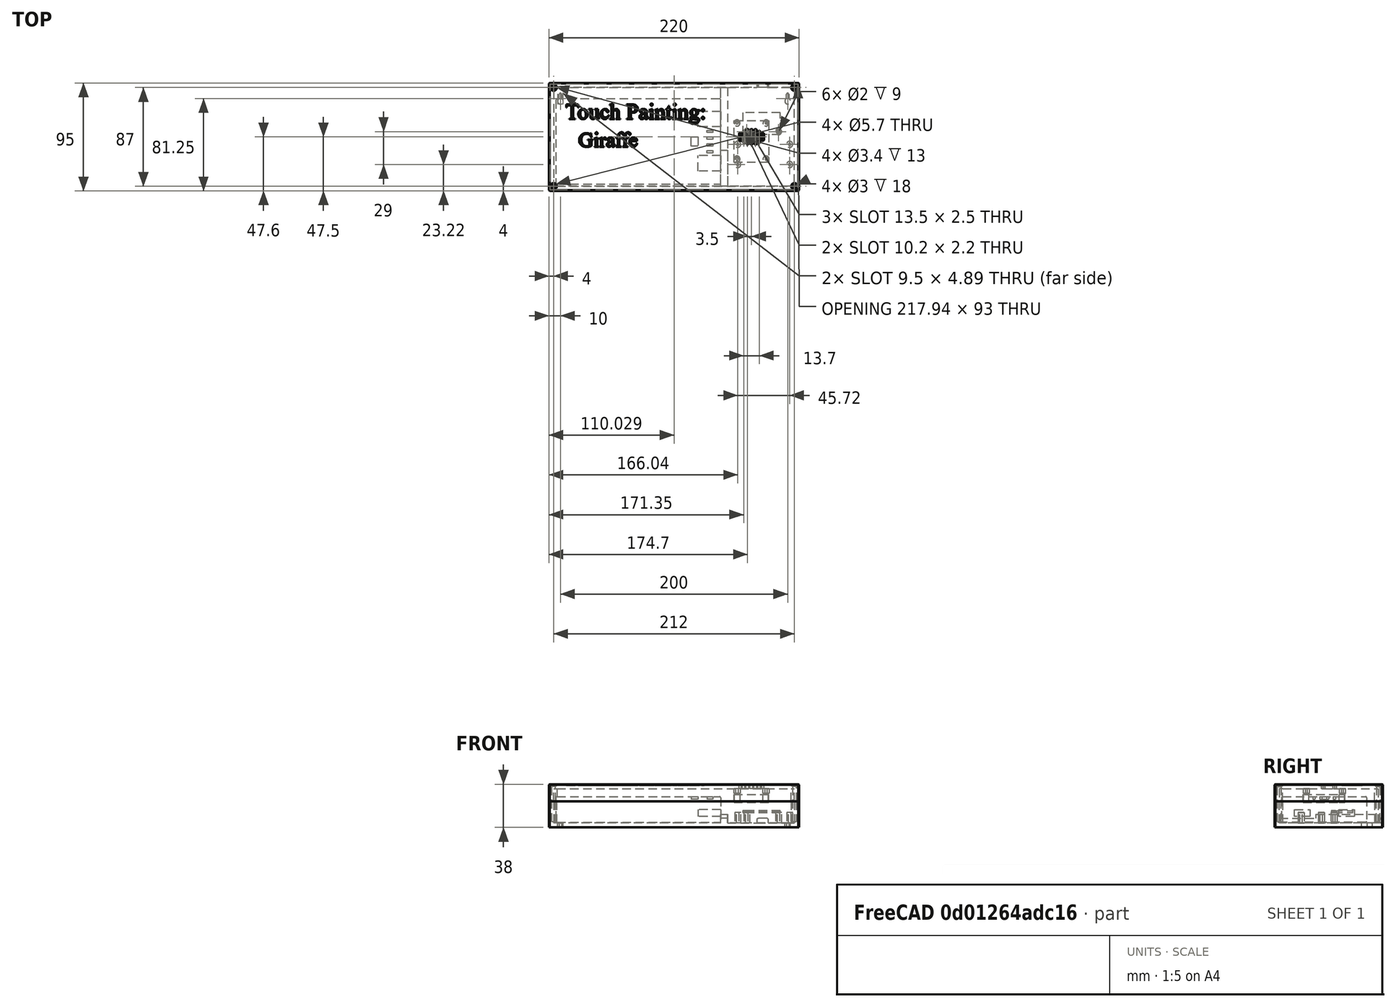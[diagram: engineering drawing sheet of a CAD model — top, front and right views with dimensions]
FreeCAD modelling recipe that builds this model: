
FCSTD DOCUMENT  (FreeCAD 0.19R24276 (Git))
Label: ShortBox
License: All rights reserved
LicenseURL: http://en.wikipedia.org/wiki/All_rights_reserved
objects: Sketcher::SketchObject×17, PartDesign::Pocket×12, PartDesign::Pad×7, PartDesign::Chamfer×4, Part::Feature×3, Mesh::Feature×2, PartDesign::Body×2, Part::Part2DObjectPython×2
note: 70 computed .brp shape members not serialized (recipe doc carries the construction recipe); baked Part::Feature solids carry a one-line shape summary decoded from their .brp

FEATURE [Part::Feature] Solid  label="MPR121 v1"
  Placement = pos=(170.5,49.7,13) rot=(0,0,1;0rad)
  shape: bbox 33.02 x 19.05 x 1.6 mm, 10 faces (baked)
FEATURE [Mesh::Feature] _062_nRF52830_Feather  label="4062-nRF52830-Feather"
  Placement = pos=(162.5,20.7,13) rot=(0,0,1;0rad)
FEATURE [Part::Feature] Solid001  label="Pocket001"
  Placement = pos=(78.6,43.5,27) rot=(1,0,0;3.14159rad)
  shape: bbox 145 x 75 x 22.5 mm, 61 faces (baked)
FEATURE [Sketcher::SketchObject] Sketch
  FullyConstrained = true
  sketch-geometry (4):
    g0: LineSegment StartX=0 StartY=0 StartZ=0 EndX=220 EndY=0 EndZ=0
    g1: LineSegment StartX=220 StartY=0 StartZ=0 EndX=220 EndY=95 EndZ=0
    g2: LineSegment StartX=220 StartY=95 StartZ=0 EndX=0 EndY=95 EndZ=0
    g3: LineSegment StartX=0 StartY=95 StartZ=0 EndX=0 EndY=0 EndZ=0
  constraints (11):
    c: Coincident(g0,g1)
    c: Coincident(g1,g2)
    c: Coincident(g2,g3)
    c: Coincident(g3,g0)
    c: Horizontal(g0)
    c: Horizontal(g2)
    c: Vertical(g1)
    c: Vertical(g3)
    c: Coincident(g0,g-1)
    c: DistanceX(g2,g2) = 220
    c: DistanceY(g1,g1) = 95
FEATURE [Part::Feature] Solid002  label="Speaker"
  Placement = pos=(178,43.4,22) rot=(0,0,1;0rad)
  shape: bbox 30.48 x 36.83 x 7 mm, 10 faces (baked)
FEATURE [PartDesign::Pad] Pad
  Direction = (1,1,1)
  Length = 23
  Length2 = 100
  Profile = -> Sketch
  Type = 0
FEATURE [Sketcher::SketchObject] Sketch001
  ExternalGeometry = -> [Pad]
  FullyConstrained = true
  MapMode = 5
  Placement = pos=(0,0,23) rot=(0,0,1;0rad)
  Support = -> [Pad]
  sketch-geometry (4):
    g0: LineSegment StartX=4 StartY=91 StartZ=0 EndX=216 EndY=91 EndZ=0
    g1: LineSegment StartX=216 StartY=91 StartZ=0 EndX=216 EndY=4 EndZ=0
    g2: LineSegment StartX=216 StartY=4 StartZ=0 EndX=4 EndY=4 EndZ=0
    g3: LineSegment StartX=4 StartY=4 StartZ=0 EndX=4 EndY=91 EndZ=0
  constraints (12):
    c: Coincident(g0,g1)
    c: Coincident(g1,g2)
    c: Coincident(g2,g3)
    c: Coincident(g3,g0)
    c: Horizontal(g0)
    c: Horizontal(g2)
    c: Vertical(g1)
    c: Vertical(g3)
    c: DistanceY(g0,g-3) = 4
    c: DistanceX(g-3,g0) = 4
    c: DistanceY(g-1,g2) = 4
    c: DistanceX(g1,g-4) = 4
FEATURE [PartDesign::Pocket] Pocket
  BaseFeature = -> Pad
  Length = 19
  Length2 = 100
  Profile = -> Sketch001
  Type = 0
FEATURE [Sketcher::SketchObject] Sketch002
  ExternalGeometry = -> [Pocket]
  FullyConstrained = true
  MapMode = 5
  Placement = pos=(0,0,4) rot=(0,0,1;0rad)
  Support = -> [Pocket]
  sketch-geometry (6):
    g0: Circle CenterX=174.04 CenterY=52.22 CenterZ=0 NormalX=0 NormalY=0 NormalZ=1 AngleXU=0 Radius=2.7
    g1: Circle CenterX=201.98 CenterY=52.22 CenterZ=0 NormalX=0 NormalY=0 NormalZ=1 AngleXU=0 Radius=2.7
    g2: Circle CenterX=166.04 CenterY=41 CenterZ=0 NormalX=0 NormalY=0 NormalZ=1 AngleXU=0 Radius=2.7
    g3: Circle CenterX=166.04 CenterY=23.22 CenterZ=0 NormalX=0 NormalY=0 NormalZ=1 AngleXU=0 Radius=2.7
    g4: Circle CenterX=211.76 CenterY=23.22 CenterZ=0 NormalX=0 NormalY=0 NormalZ=1 AngleXU=0 Radius=2.7
    g5: Circle CenterX=211.76 CenterY=41 CenterZ=0 NormalX=0 NormalY=0 NormalZ=1 AngleXU=0 Radius=2.7
  constraints (18):
    c: DistanceX(g5,g-5) = 4.24
    c: DistanceY(g5,g-5) = 50
    c: Radius(g5) = 2.7
    c: Radius(g2) = 2.7
    c: Radius(g3) = 2.7
    c: Radius(g4) = 2.7
    c: DistanceX(g2,g3) = 0
    c: DistanceY(g3,g4) = 0
    c: DistanceY(g5,g2) = 0
    c: DistanceX(g2,g5) = 45.72
    c: DistanceY(g3,g2) = 17.78
    c: Radius(g0) = 2.7
    c: Radius(g1) = 2.7
    c: DistanceY(g0,g1) = 0
    c: DistanceX(g0,g1) = 27.94
    c: DistanceY(g2,g0) = 11.22
    c: DistanceX(g4,g5) = 0
    c: DistanceX(g0,g2) = -8
FEATURE [PartDesign::Pad] Pad001  label="BoardPosts"
  BaseFeature = -> Pocket
  Direction = (1,1,1)
  Length = 9
  Length2 = 100
  Profile = -> Sketch002
  Type = 0
FEATURE [Sketcher::SketchObject] Sketch003
  ExternalGeometry = -> [Pad001]
  FullyConstrained = true
  MapMode = 5
  Placement = pos=(0,0,13) rot=(0,0,1;0rad)
  Support = -> [Pad001]
  sketch-geometry (6):
    g0: Circle CenterX=166.04 CenterY=41 CenterZ=0 NormalX=0 NormalY=0 NormalZ=1 AngleXU=0 Radius=1
    g1: Circle CenterX=211.76 CenterY=41 CenterZ=0 NormalX=0 NormalY=0 NormalZ=1 AngleXU=0 Radius=1
    g2: Circle CenterX=211.76 CenterY=23.22 CenterZ=0 NormalX=0 NormalY=0 NormalZ=1 AngleXU=0 Radius=1
    g3: Circle CenterX=166.04 CenterY=23.22 CenterZ=0 NormalX=0 NormalY=0 NormalZ=1 AngleXU=0 Radius=1
    g4: Circle CenterX=174.04 CenterY=52.22 CenterZ=0 NormalX=0 NormalY=0 NormalZ=1 AngleXU=0 Radius=1
    g5: Circle CenterX=201.98 CenterY=52.22 CenterZ=0 NormalX=0 NormalY=0 NormalZ=1 AngleXU=0 Radius=1
  constraints (12):
    c: Coincident(g0,g-6)
    c: Coincident(g1,g-5)
    c: Coincident(g2,g-8)
    c: Coincident(g3,g-7)
    c: Coincident(g4,g-3)
    c: Coincident(g5,g-4)
    c: Radius(g4) = 1
    c: Radius(g5) = 1
    c: Radius(g1) = 1
    c: Radius(g0) = 1
    c: Radius(g3) = 1
    c: Radius(g2) = 1
FEATURE [PartDesign::Pocket] Pocket001  label="BoardPostHoles"
  BaseFeature = -> Pad001
  Length = 9
  Length2 = 100
  Profile = -> Sketch003
  Type = 0
FEATURE [Sketcher::SketchObject] Sketch004
  ExternalGeometry = -> [Pocket001]
  FullyConstrained = true
  MapMode = 5
  Placement = pos=(0,95,0) rot=(0,0.707107,0.707107;3.14159rad)
  Support = -> [Pocket001]
  sketch-geometry (4):
    g0: LineSegment StartX=-193.01 StartY=8 StartZ=0 EndX=-183.01 EndY=8 EndZ=0
    g1: LineSegment StartX=-183.01 StartY=8 StartZ=0 EndX=-183.01 EndY=4 EndZ=0
    g2: LineSegment StartX=-183.01 StartY=4 StartZ=0 EndX=-193.01 EndY=4 EndZ=0
    g3: LineSegment StartX=-193.01 StartY=4 StartZ=0 EndX=-193.01 EndY=8 EndZ=0
  constraints (13):
    c: Coincident(g0,g1)
    c: Coincident(g1,g2)
    c: Coincident(g2,g3)
    c: Coincident(g3,g0)
    c: Horizontal(g0)
    c: Horizontal(g2)
    c: Vertical(g1)
    c: Vertical(g3)
    c: PointOnObject(g1,g-3)
    c: DistanceX(g0,g0) = 10
    c: DistanceX(g-5,g-6) = 22.54
    c: DistanceX(g-5,g0) = 6.27
    c: DistanceY(g1,g1) = 4
FEATURE [PartDesign::Pocket] Pocket002  label="PaintingWires"
  BaseFeature = -> Pocket001
  Length = 4
  Length2 = 100
  Profile = -> Sketch004
  Type = 0
FEATURE [PartDesign::Chamfer] Chamfer
  Angle = 45
  Base = -> Pocket002 [Edge34,Edge33]
  BaseFeature = -> Pocket002
  ChamferType = 0
  FlipDirection = false
  Size = 1
  Size2 = 1
  SupportTransform = false
FEATURE [Mesh::Feature] TalenCell_battery_pack
  Placement = pos=(5,154,-68) rot=(1,0,0;1.5708rad)
FEATURE [Sketcher::SketchObject] Sketch006
  FullyConstrained = false
  MapMode = 5
  Placement = pos=(0,0,4) rot=(0,0,1;0rad)
  sketch-geometry (4):
    g0: LineSegment StartX=151 StartY=91 StartZ=0 EndX=157 EndY=91 EndZ=0
    g1: LineSegment StartX=157 StartY=91 StartZ=0 EndX=157 EndY=3.51944 EndZ=0
    g2: LineSegment StartX=157 StartY=3.51944 StartZ=0 EndX=151 EndY=3.51944 EndZ=0
    g3: LineSegment StartX=151 StartY=3.51944 StartZ=0 EndX=151 EndY=91 EndZ=0
  constraints (9):
    c: Coincident(g0,g1)
    c: Coincident(g1,g2)
    c: Coincident(g2,g3)
    c: Coincident(g3,g0)
    c: Horizontal(g0)
    c: Horizontal(g2)
    c: Vertical(g1)
    c: Vertical(g3)
    c: DistanceX(g0,g0) = 6
FEATURE [PartDesign::Pad] Pad002  label="BatDivider"
  BaseFeature = -> Chamfer
  Direction = (1,1,1)
  Length = 7.5
  Length2 = 100
  Profile = -> Sketch006
  Type = 0
FEATURE [Sketcher::SketchObject] Sketch007
  ExternalGeometry = -> [Pad002]
  FullyConstrained = true
  MapMode = 5
  Placement = pos=(0,0,11.5) rot=(0,0,1;0rad)
  Support = -> [Pad002]
  sketch-geometry (4):
    g0: LineSegment StartX=151 StartY=36 StartZ=0 EndX=157 EndY=36 EndZ=0
    g1: LineSegment StartX=157 StartY=36 StartZ=0 EndX=157 EndY=4 EndZ=0
    g2: LineSegment StartX=157 StartY=4 StartZ=0 EndX=151 EndY=4 EndZ=0
    g3: LineSegment StartX=151 StartY=4 StartZ=0 EndX=151 EndY=36 EndZ=0
  constraints (11):
    c: Coincident(g0,g1)
    c: Coincident(g1,g2)
    c: Coincident(g2,g3)
    c: Coincident(g3,g0)
    c: Horizontal(g0)
    c: Horizontal(g2)
    c: Vertical(g1)
    c: Vertical(g3)
    c: PointOnObject(g0,g-3)
    c: Coincident(g1,g-4)
    c: DistanceY(g1,g1) = 32
FEATURE [PartDesign::Pocket] Pocket003  label="BatDividerUsbCutout"
  BaseFeature = -> Pad002
  Length = 3.5
  Length2 = 100
  Profile = -> Sketch007
  Type = 0
FEATURE [Sketcher::SketchObject] Sketch008
  ExternalGeometry = -> [Pocket003]
  FullyConstrained = false
  MapMode = 5
  Placement = pos=(0,0,4) rot=(0,0,1;0rad)
  Support = -> [Pocket003]
  sketch-geometry (8):
    g0: ArcOfCircle CenterX=10 CenterY=85 CenterZ=0 NormalX=0 NormalY=0 NormalZ=1 AngleXU=0 Radius=1 StartAngle=0 EndAngle=3.14159
    g1: ArcOfCircle CenterX=10 CenterY=79 CenterZ=0 NormalX=0 NormalY=0 NormalZ=1 AngleXU=0 Radius=2.5 StartAngle=1.98231 EndAngle=7.44246
    g2: LineSegment StartX=11 StartY=85 StartZ=0 EndX=11 EndY=81.2913 EndZ=0
    g3: LineSegment StartX=9 StartY=81.2913 StartZ=0 EndX=9 EndY=85 EndZ=0
    g4: ArcOfCircle CenterX=210 CenterY=85 CenterZ=0 NormalX=0 NormalY=0 NormalZ=1 AngleXU=0 Radius=1 StartAngle=0 EndAngle=3.14159
    g5: ArcOfCircle CenterX=210 CenterY=79 CenterZ=0 NormalX=0 NormalY=0 NormalZ=1 AngleXU=0 Radius=2.5 StartAngle=1.98231 EndAngle=7.44246
    g6: LineSegment StartX=211 StartY=85 StartZ=0 EndX=211 EndY=81.2913 EndZ=0
    g7: LineSegment StartX=209 StartY=81.2913 StartZ=0 EndX=209 EndY=85 EndZ=0
  constraints (25):
    c: Vertical(g2)
    c: Vertical(g3)
    c: Radius(g0) = 1
    c: Radius(g1) = 2.5
    c: DistanceX(g3,g2) = 2
    c: DistanceY(g2,g0) = 0
    c: DistanceX(g3,g0) = 1
    c: DistanceY(g1,g0) = 6
    c: DistanceX(g0,g1) = 0
    c: DistanceY(g0,g-4) = 6
    c: DistanceX(g-4,g0) = 6
    c: Coincident(g1,g3)
    c: Coincident(g1,g2)
    c: Vertical(g6)
    c: Vertical(g7)
    c: DistanceY(g7,g4) = 0
    c: Radius(g5) = 2.5
    c: Radius(g4) = 1
    c: DistanceX(g7,g6) = 2
    c: DistanceX(g7,g4) = 1
    c: DistanceY(g5,g4) = 6
    c: DistanceY(g4,g-6) = 6
    c: DistanceX(g4,g-6) = 6
    c: Coincident(g5,g7)
    c: Coincident(g5,g6)
FEATURE [PartDesign::Pocket] Pocket004  label="HangerHoles"
  BaseFeature = -> Pocket003
  Length = 4
  Length2 = 100
  Profile = -> Sketch008
  Type = 0
FEATURE [Sketcher::SketchObject] Sketch009
  ExternalGeometry = -> [Pocket004]
  FullyConstrained = true
  MapMode = 5
  Placement = pos=(0,0,4) rot=(0,0,1;0rad)
  Support = -> [Pocket004]
  sketch-geometry (4):
    g0: Circle CenterX=4 CenterY=91 CenterZ=0 NormalX=0 NormalY=0 NormalZ=1 AngleXU=0 Radius=3
    g1: Circle CenterX=4 CenterY=4 CenterZ=0 NormalX=0 NormalY=0 NormalZ=1 AngleXU=0 Radius=3
    g2: Circle CenterX=216 CenterY=4 CenterZ=0 NormalX=0 NormalY=0 NormalZ=1 AngleXU=0 Radius=3
    g3: Circle CenterX=216 CenterY=91 CenterZ=0 NormalX=0 NormalY=0 NormalZ=1 AngleXU=0 Radius=3
  constraints (8):
    c: Coincident(g0,g-4)
    c: Radius(g0) = 3
    c: Coincident(g1,g-4)
    c: Radius(g1) = 3
    c: Coincident(g2,g-5)
    c: Radius(g2) = 3
    c: Coincident(g3,g-5)
    c: Radius(g3) = 3
FEATURE [PartDesign::Pad] Pad003  label="TopMountingPosts"
  BaseFeature = -> Pocket004
  Direction = (1,1,1)
  Length = 19
  Length2 = 100
  Profile = -> Sketch009
  Type = 0
FEATURE [Sketcher::SketchObject] Sketch010
  ExternalGeometry = -> [Pad003]
  FullyConstrained = true
  MapMode = 5
  Placement = pos=(0,0,23) rot=(0,0,1;0rad)
  Support = -> [Pad003]
  sketch-geometry (4):
    g0: Circle CenterX=216 CenterY=91 CenterZ=0 NormalX=0 NormalY=0 NormalZ=1 AngleXU=0 Radius=1.5
    g1: Circle CenterX=216 CenterY=4 CenterZ=0 NormalX=0 NormalY=0 NormalZ=1 AngleXU=0 Radius=1.5
    g2: Circle CenterX=4 CenterY=4 CenterZ=0 NormalX=0 NormalY=0 NormalZ=1 AngleXU=0 Radius=1.5
    g3: Circle CenterX=4 CenterY=91 CenterZ=0 NormalX=0 NormalY=0 NormalZ=1 AngleXU=0 Radius=1.5
  constraints (8):
    c: Coincident(g0,g-5)
    c: Coincident(g1,g-6)
    c: Coincident(g2,g-4)
    c: Coincident(g3,g-3)
    c: Radius(g3) = 1.5
    c: Radius(g2) = 1.5
    c: Radius(g1) = 1.5
    c: Radius(g0) = 1.5
FEATURE [PartDesign::Pocket] Pocket005  label="TopMountingHoles"
  BaseFeature = -> Pad003
  Length = 18
  Length2 = 100
  Profile = -> Sketch010
  Type = 0
FEATURE [Sketcher::SketchObject] Sketch011
  FullyConstrained = true
  MapMode = 5
  Support = -> [XY_Plane001]
  sketch-geometry (4):
    g0: LineSegment StartX=0 StartY=95 StartZ=0 EndX=220 EndY=95 EndZ=0
    g1: LineSegment StartX=220 StartY=95 StartZ=0 EndX=220 EndY=0 EndZ=0
    g2: LineSegment StartX=220 StartY=0 StartZ=0 EndX=0 EndY=0 EndZ=0
    g3: LineSegment StartX=0 StartY=0 StartZ=0 EndX=0 EndY=95 EndZ=0
  constraints (12):
    c: Coincident(g0,g1)
    c: Coincident(g1,g2)
    c: Coincident(g2,g3)
    c: Coincident(g3,g0)
    c: Horizontal(g0)
    c: Horizontal(g2)
    c: Vertical(g1)
    c: Vertical(g3)
    c: PointOnObject(g0,g-2)
    c: DistanceX(g0,g0) = 220
    c: DistanceY(g3,g3) = 95
    c: DistanceY(g2,g-1) = 0
FEATURE [PartDesign::Pad] Pad004
  Direction = (1,1,1)
  Length = 15
  Length2 = 100
  Profile = -> Sketch011
  Type = 0
FEATURE [Sketcher::SketchObject] Sketch012
  ExternalGeometry = -> [Pad004]
  FullyConstrained = true
  MapMode = 5
  Placement = pos=(0,0,0) rot=(1,0,0;3.14159rad)
  Support = -> [Pad004]
  sketch-geometry (4):
    g0: LineSegment StartX=4 StartY=-4 StartZ=0 EndX=216 EndY=-4 EndZ=0
    g1: LineSegment StartX=216 StartY=-4 StartZ=0 EndX=216 EndY=-91 EndZ=0
    g2: LineSegment StartX=216 StartY=-91 StartZ=0 EndX=4 EndY=-91 EndZ=0
    g3: LineSegment StartX=4 StartY=-91 StartZ=0 EndX=4 EndY=-4 EndZ=0
  constraints (13):
    c: Coincident(g0,g1)
    c: Coincident(g1,g2)
    c: Coincident(g2,g3)
    c: Coincident(g3,g0)
    c: Horizontal(g0)
    c: Horizontal(g2)
    c: Vertical(g1)
    c: Vertical(g3)
    c: DistanceY(g0,g-1) = 4
    c: DistanceY(g-3,g1) = 4
    c: DistanceX(g-4,g2) = 4
    c: DistanceX(g-3,g-3) = 0
    c: DistanceX(g0,g-3) = 4
FEATURE [PartDesign::Pocket] Pocket006
  BaseFeature = -> Pad004
  Length = 11
  Length2 = 100
  Profile = -> Sketch012
  Type = 0
FEATURE [Sketcher::SketchObject] Sketch013
  ExternalGeometry = -> [Pocket006]
  FullyConstrained = true
  MapMode = 5
  Placement = pos=(0,0,11) rot=(1,0,0;3.14159rad)
  Support = -> [Pocket006]
  sketch-geometry (4):
    g0: Circle CenterX=4 CenterY=-91 CenterZ=0 NormalX=0 NormalY=0 NormalZ=1 AngleXU=0 Radius=3
    g1: Circle CenterX=4 CenterY=-4 CenterZ=0 NormalX=0 NormalY=0 NormalZ=1 AngleXU=0 Radius=3
    g2: Circle CenterX=216 CenterY=-91 CenterZ=0 NormalX=0 NormalY=0 NormalZ=1 AngleXU=0 Radius=3
    g3: Circle CenterX=216 CenterY=-4 CenterZ=0 NormalX=0 NormalY=0 NormalZ=1 AngleXU=0 Radius=3
  constraints (8):
    c: Coincident(g0,g-4)
    c: Coincident(g1,g-3)
    c: Radius(g1) = 3
    c: Radius(g0) = 3
    c: Coincident(g2,g-4)
    c: Coincident(g3,g-3)
    c: Radius(g3) = 3
    c: Radius(g2) = 3
FEATURE [PartDesign::Pad] Pad005  label="TopMountingPost"
  BaseFeature = -> Pocket006
  Direction = (1,1,1)
  Length = 11
  Length2 = 100
  Profile = -> Sketch013
  Type = 0
FEATURE [Sketcher::SketchObject] Sketch014
  ExternalGeometry = -> [Pad005]
  FullyConstrained = true
  MapMode = 5
  Placement = pos=(0,0,0) rot=(1,0,0;3.14159rad)
  Support = -> [Pad005]
  sketch-geometry (4):
    g0: Circle CenterX=216 CenterY=-4 CenterZ=0 NormalX=0 NormalY=0 NormalZ=1 AngleXU=0 Radius=1.7
    g1: Circle CenterX=216 CenterY=-91 CenterZ=0 NormalX=0 NormalY=0 NormalZ=1 AngleXU=0 Radius=1.7
    g2: Circle CenterX=4 CenterY=-91 CenterZ=0 NormalX=0 NormalY=0 NormalZ=1 AngleXU=0 Radius=1.7
    g3: Circle CenterX=4 CenterY=-4 CenterZ=0 NormalX=0 NormalY=0 NormalZ=1 AngleXU=0 Radius=1.7
  constraints (8):
    c: Coincident(g0,g-6)
    c: Coincident(g1,g-5)
    c: Coincident(g2,g-4)
    c: Coincident(g3,g-3)
    c: Radius(g3) = 1.7
    c: Radius(g2) = 1.7
    c: Radius(g1) = 1.7
    c: Radius(g0) = 1.7
FEATURE [PartDesign::Pocket] Pocket007  label="TopMountingHoles001"
  BaseFeature = -> Pad005
  Length = 15
  Length2 = 100
  Profile = -> Sketch014
  Type = 0
FEATURE [Sketcher::SketchObject] Sketch015
  ExternalGeometry = -> [Pocket007]
  FullyConstrained = true
  MapMode = 5
  Placement = pos=(0,0,15) rot=(0,0,1;0rad)
  Support = -> [Pocket007]
  sketch-geometry (4):
    g0: Circle CenterX=4 CenterY=4 CenterZ=0 NormalX=0 NormalY=0 NormalZ=1 AngleXU=0 Radius=2.85
    g1: Circle CenterX=4 CenterY=91 CenterZ=0 NormalX=0 NormalY=0 NormalZ=1 AngleXU=0 Radius=2.85
    g2: Circle CenterX=216 CenterY=91 CenterZ=0 NormalX=0 NormalY=0 NormalZ=1 AngleXU=0 Radius=2.85
    g3: Circle CenterX=216 CenterY=4 CenterZ=0 NormalX=0 NormalY=0 NormalZ=1 AngleXU=0 Radius=2.85
  constraints (8):
    c: Coincident(g0,g-6)
    c: Radius(g0) = 2.85
    c: Coincident(g1,g-3)
    c: Radius(g1) = 2.85
    c: Coincident(g2,g-4)
    c: Radius(g2) = 2.85
    c: Coincident(g3,g-5)
    c: Radius(g3) = 2.85
FEATURE [PartDesign::Pocket] Pocket008  label="TopMountingHolesHead"
  BaseFeature = -> Pocket007
  Length = 2
  Length2 = 100
  Profile = -> Sketch015
  Type = 0
FEATURE [PartDesign::Chamfer] Chamfer001  label="TopMountingHolesHeadChamf"
  Angle = 45
  Base = -> Pocket008 [Edge60,Edge58,Edge54,Edge56]
  BaseFeature = -> Pocket008
  ChamferType = 0
  FlipDirection = false
  Size = 1.1
  Size2 = 1
  SupportTransform = false
FEATURE [Sketcher::SketchObject] Sketch016
  ExternalGeometry = -> [Chamfer001]
  FullyConstrained = true
  MapMode = 5
  Placement = pos=(0,0,11) rot=(1,0,0;3.14159rad)
  Support = -> [Chamfer001]
  sketch-geometry (8):
    g0: Circle CenterX=165.4 CenterY=-28 CenterZ=0 NormalX=0 NormalY=0 NormalZ=1 AngleXU=0 Radius=2.7
    g1: Circle CenterX=191 CenterY=-28 CenterZ=0 NormalX=0 NormalY=0 NormalZ=1 AngleXU=0 Radius=2.7
    g2: Circle CenterX=191 CenterY=-59.8 CenterZ=0 NormalX=0 NormalY=0 NormalZ=1 AngleXU=0 Radius=2.7
    g3: Circle CenterX=165.4 CenterY=-59.8 CenterZ=0 NormalX=0 NormalY=0 NormalZ=1 AngleXU=0 Radius=2.7
    g4: Circle CenterX=165.4 CenterY=-28 CenterZ=0 NormalX=0 NormalY=0 NormalZ=1 AngleXU=0 Radius=0.9
    g5: Circle CenterX=191 CenterY=-28 CenterZ=0 NormalX=0 NormalY=0 NormalZ=1 AngleXU=0 Radius=0.9
    g6: Circle CenterX=191 CenterY=-59.8 CenterZ=0 NormalX=0 NormalY=0 NormalZ=1 AngleXU=0 Radius=0.9
    g7: Circle CenterX=165.4 CenterY=-59.8 CenterZ=0 NormalX=0 NormalY=0 NormalZ=1 AngleXU=0 Radius=0.9
  constraints (20):
    c: Radius(g0) = 2.7
    c: Radius(g1) = 2.7
    c: Radius(g3) = 2.7
    c: Radius(g2) = 2.7
    c: Coincident(g4,g0)
    c: Coincident(g5,g1)
    c: Coincident(g6,g2)
    c: Coincident(g7,g3)
    c: Radius(g4) = 0.9
    c: Radius(g5) = 0.9
    c: Radius(g7) = 0.9
    c: Radius(g6) = 0.9
    c: DistanceX(g0,g3) = 0
    c: DistanceX(g1,g2) = 0
    c: DistanceY(g3,g2) = 0
    c: DistanceY(g0,g1) = 0
    c: DistanceX(g0,g1) = 25.6
    c: DistanceY(g3,g0) = 31.8
    c: DistanceX(g1,g-3) = 25
    c: DistanceY(g1,g-3) = 24
FEATURE [PartDesign::Pad] Pad006  label="SpeakerPosts"
  BaseFeature = -> Chamfer001
  Direction = (1,1,1)
  Length = 4
  Length2 = 100
  Profile = -> Sketch016
  Type = 0
FEATURE [Sketcher::SketchObject] Sketch017
  ExternalGeometry = -> [Pad006]
  FullyConstrained = true
  MapMode = 5
  Placement = pos=(0,0,11) rot=(1,0,0;3.14159rad)
  Support = -> [Pad006]
  sketch-geometry (28):
    g0: ArcOfCircle CenterX=171.35 CenterY=-43.6 CenterZ=0 NormalX=0 NormalY=0 NormalZ=1 AngleXU=0 Radius=1.1 StartAngle=8e-16 EndAngle=3.14159
    g1: ArcOfCircle CenterX=171.35 CenterY=-51.6 CenterZ=0 NormalX=0 NormalY=0 NormalZ=1 AngleXU=0 Radius=1.1 StartAngle=3.14159 EndAngle=6.28319
    g2: LineSegment StartX=170.25 StartY=-43.6 StartZ=0 EndX=170.25 EndY=-51.6 EndZ=0
    g3: LineSegment StartX=172.45 StartY=-43.6 StartZ=0 EndX=172.45 EndY=-51.6 EndZ=0
    g4: ArcOfCircle CenterX=178.2 CenterY=-42.1 CenterZ=0 NormalX=0 NormalY=0 NormalZ=1 AngleXU=0 Radius=1.25 StartAngle=-1.8e-15 EndAngle=3.14159
    g5: ArcOfCircle CenterX=178.2 CenterY=-53.1 CenterZ=0 NormalX=0 NormalY=0 NormalZ=1 AngleXU=0 Radius=1.25 StartAngle=3.14159 EndAngle=6.28319
    g6: LineSegment StartX=176.95 StartY=-42.1 StartZ=0 EndX=176.95 EndY=-53.1 EndZ=0
    g7: LineSegment StartX=179.45 StartY=-42.1 StartZ=0 EndX=179.45 EndY=-53.1 EndZ=0
    g8: ArcOfCircle CenterX=185.05 CenterY=-43.6 CenterZ=0 NormalX=0 NormalY=0 NormalZ=1 AngleXU=0 Radius=1.1 StartAngle=-2.7e-15 EndAngle=3.14159
    g9: ArcOfCircle CenterX=185.05 CenterY=-51.6 CenterZ=0 NormalX=0 NormalY=0 NormalZ=1 AngleXU=0 Radius=1.1 StartAngle=3.14159 EndAngle=6.28319
    g10: LineSegment StartX=183.95 StartY=-43.6 StartZ=0 EndX=183.95 EndY=-51.6 EndZ=0
    g11: LineSegment StartX=186.15 StartY=-43.6 StartZ=0 EndX=186.15 EndY=-51.6 EndZ=0
    g12: ArcOfCircle CenterX=168.25 CenterY=-45.1 CenterZ=0 NormalX=0 NormalY=0 NormalZ=1 AngleXU=0 Radius=1 StartAngle=1.7e-15 EndAngle=3.14159
    g13: ArcOfCircle CenterX=168.25 CenterY=-50.1 CenterZ=0 NormalX=0 NormalY=0 NormalZ=1 AngleXU=0 Radius=1 StartAngle=3.14159 EndAngle=6.28319
    g14: LineSegment StartX=167.25 StartY=-45.1 StartZ=0 EndX=167.25 EndY=-50.1 EndZ=0
    g15: LineSegment StartX=169.25 StartY=-45.1 StartZ=0 EndX=169.25 EndY=-50.1 EndZ=0
    g16: ArcOfCircle CenterX=188.15 CenterY=-45.1 CenterZ=0 NormalX=0 NormalY=0 NormalZ=1 AngleXU=0 Radius=1 StartAngle=9e-16 EndAngle=3.14159
    g17: ArcOfCircle CenterX=188.15 CenterY=-50.1 CenterZ=0 NormalX=0 NormalY=0 NormalZ=1 AngleXU=0 Radius=1 StartAngle=3.14159 EndAngle=6.28319
    g18: LineSegment StartX=187.15 StartY=-45.1 StartZ=0 EndX=187.15 EndY=-50.1 EndZ=0
    g19: LineSegment StartX=189.15 StartY=-45.1 StartZ=0 EndX=189.15 EndY=-50.1 EndZ=0
    g20: ArcOfCircle CenterX=174.7 CenterY=-42.1 CenterZ=0 NormalX=0 NormalY=0 NormalZ=1 AngleXU=0 Radius=1.25 StartAngle=2.2e-15 EndAngle=3.14159
    g21: ArcOfCircle CenterX=174.7 CenterY=-53.1 CenterZ=0 NormalX=0 NormalY=0 NormalZ=1 AngleXU=0 Radius=1.25 StartAngle=3.14159 EndAngle=6.28319
    g22: LineSegment StartX=173.45 StartY=-42.1 StartZ=0 EndX=173.45 EndY=-53.1 EndZ=0
    g23: LineSegment StartX=175.95 StartY=-42.1 StartZ=0 EndX=175.95 EndY=-53.1 EndZ=0
    g24: ArcOfCircle CenterX=181.7 CenterY=-42.1 CenterZ=0 NormalX=0 NormalY=0 NormalZ=1 AngleXU=0 Radius=1.25 StartAngle=1e-15 EndAngle=3.14159
    g25: ArcOfCircle CenterX=181.7 CenterY=-53.1 CenterZ=0 NormalX=0 NormalY=0 NormalZ=1 AngleXU=0 Radius=1.25 StartAngle=3.14159 EndAngle=6.28319
    g26: LineSegment StartX=180.45 StartY=-42.1 StartZ=0 EndX=180.45 EndY=-53.1 EndZ=0
    g27: LineSegment StartX=182.95 StartY=-42.1 StartZ=0 EndX=182.95 EndY=-53.1 EndZ=0
  constraints (71):
    c: Tangent(g0,g3) = 1.5708
    c: Tangent(g0,g2) = -1.5708
    c: Tangent(g2,g1) = -1.5708
    c: Tangent(g3,g1) = 1.5708
    c: Vertical(g2)
    c: Equal(g0,g1)
    c: Tangent(g4,g7) = 1.5708
    c: Tangent(g4,g6) = -1.5708
    c: Tangent(g6,g5) = -1.5708
    c: Tangent(g7,g5) = 1.5708
    c: Vertical(g6)
    c: Equal(g4,g5)
    c: Tangent(g8,g11) = 1.5708
    c: Tangent(g8,g10) = -1.5708
    c: Tangent(g10,g9) = -1.5708
    c: Tangent(g11,g9) = 1.5708
    c: Vertical(g10)
    c: Equal(g8,g9)
    c: DistanceX(g1,g1) = 2.2
    c: DistanceX(g5,g5) = 2.5
    c: DistanceX(g9,g9) = 2.2
    c: Tangent(g12,g15) = 1.5708
    c: Tangent(g12,g14) = -1.5708
    c: Tangent(g14,g13) = -1.5708
    c: Tangent(g15,g13) = 1.5708
    c: Vertical(g14)
    c: Equal(g12,g13)
    c: Tangent(g16,g19) = 1.5708
    c: Tangent(g16,g18) = -1.5708
    c: Tangent(g18,g17) = -1.5708
    c: Tangent(g19,g17) = 1.5708
    c: Vertical(g18)
    c: Equal(g16,g17)
    c: DistanceX(g13,g13) = 2
    c: DistanceX(g17,g17) = 2
    c: DistanceY(g12,g0) = 1.5
    c: DistanceY(g1,g13) = 1.5
    c: DistanceY(g9,g17) = 1.5
    c: DistanceY(g16,g8) = 1.5
    c: Tangent(g20,g23) = 1.5708
    c: Tangent(g20,g22) = -1.5708
    c: Tangent(g22,g21) = -1.5708
    c: Tangent(g23,g21) = 1.5708
    c: Vertical(g22)
    c: Equal(g20,g21)
    c: Tangent(g24,g27) = 1.5708
    c: Tangent(g24,g26) = -1.5708
    c: Tangent(g26,g25) = -1.5708
    c: Tangent(g27,g25) = 1.5708
    c: Vertical(g26)
    c: Equal(g24,g25)
    c: DistanceX(g21,g21) = 2.5
    c: DistanceX(g25,g25) = 2.5
    c: DistanceY(g8,g24) = 1.5
    c: DistanceY(g25,g9) = 1.5
    c: DistanceY(g21,g1) = 1.5
    c: DistanceY(g20,g0) = -1.5
    c: DistanceY(g4,g20) = 0
    c: DistanceY(g21,g5) = 0
    c: DistanceY(g24,g4) = 0
    c: DistanceY(g5,g25) = 0
    c: DistanceX(g12,g0) = 1
    c: DistanceX(g0,g20) = 1
    c: DistanceX(g20,g4) = 1
    c: DistanceX(g4,g24) = 1
    c: DistanceX(g24,g8) = 1
    c: DistanceX(g8,g16) = 1
    c: DistanceY(g-3,g21) = 6.7
    c: DistanceX(g-3,g-6) = 25.6
    c: DistanceX(g-3,g5) = 12.8
    c: DistanceY(g5,g4) = 11
FEATURE [PartDesign::Pocket] Pocket009  label="SpeakerVents"
  BaseFeature = -> Pad006
  Length = 4
  Length2 = 100
  Profile = -> Sketch017
  Type = 0
FEATURE [PartDesign::Chamfer] Chamfer002  label="OutsideEdgesChamfTop"
  Angle = 45
  Base = -> Pocket009 [Edge45,Edge7,Edge42,Edge9,Edge6,Edge43,Edge8,Edge47]
  BaseFeature = -> Pocket009
  ChamferType = 0
  FlipDirection = false
  Size = 0.5
  Size2 = 1
  SupportTransform = false
FEATURE [PartDesign::Chamfer] Chamfer003  label="OutsideEdgesChamfBot"
  Angle = 45
  Base = -> Pocket005 [Edge10,Edge48,Edge7,Edge23]
  BaseFeature = -> Pocket005
  ChamferType = 0
  FlipDirection = false
  Size = 0.5
  Size2 = 1
  SupportTransform = false
FEATURE [PartDesign::Body] Body  label="BoxBottom"
  Group = -> [Sketch,Pad,Sketch001,Pocket,Sketch002,Pad001,Sketch003,Pocket001,Sketch004,Pocket002,Chamfer,Sketch006,Pad002,Sketch007,Pocket003,Sketch008,Pocket004,Sketch009,Pad003,Sketch010,Pocket005,Chamfer003]
  Origin = -> Origin
  Tip = -> Chamfer003
FEATURE [Part::Part2DObjectPython] ShapeString  label="Text-TouchPainting001"  # Draft 2D object (typed FeaturePython)
  FontFile = <path>
  Placement = pos=(14.48,63.13,15) rot=(0,0,1;0rad)
  Size = 15
  String = Touch Painting:
  Tracking = 0
FEATURE [PartDesign::Pocket] Pocket010  label="Text-TouchPainting"
  BaseFeature = -> Chamfer002
  Length = 1.2
  Length2 = 100
  Profile = -> ShapeString
  Type = 0
FEATURE [Part::Part2DObjectPython] ShapeString001  label="Text-DartFrog001"  # Draft 2D object (typed FeaturePython)
  FontFile = <path>
  Placement = pos=(25.85,38.7,15) rot=(0,0,1;0rad)
  Size = 14
  String = Giraffe
  Tracking = 0
FEATURE [PartDesign::Pocket] Pocket011  label="Text-DartFrog"
  BaseFeature = -> Pocket010
  Length = 1.2
  Length2 = 100
  Profile = -> ShapeString001
  Type = 0
FEATURE [PartDesign::Body] Body001  label="BoxTop"
  Group = -> [Sketch011,Pad004,Sketch012,Pocket006,Sketch013,Pad005,Sketch014,Pocket007,Sketch015,Pocket008,Chamfer001,Sketch016,Pad006,Sketch017,Pocket009,Chamfer002,ShapeString,Pocket010,ShapeString001,Pocket011]
  Origin = -> Origin001
  Placement = pos=(0,0,23) rot=(0,0,1;0rad)
  Tip = -> Pocket011
note: 2 file-system paths scrubbed to <path> (originals preserved in the JSON sidecar)
